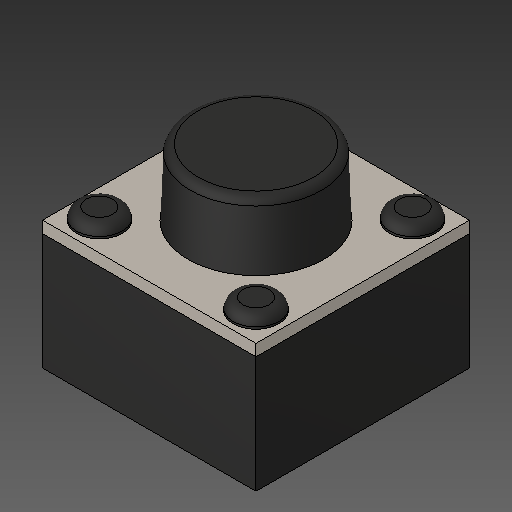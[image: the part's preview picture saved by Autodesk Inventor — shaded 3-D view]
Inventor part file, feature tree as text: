
AUTODESK INVENTOR PART (.ipt)
format: ipt  version: 2018.2 (Build 222227000, 227)  size: 160,256 bytes
history: native  units: mm
features: other x4, fillet x2
ambient origin geometry x8: Origin, YZ Plane, XZ Plane, XY Plane, X Axis, Y Axis, Z Axis, Center Point
bodies: Body1 (feature_tree), Body2 (feature_tree), Body3 (feature_tree)
feature tree (6):
  other  "ソリッド1"
  other  "ソリッド2"
  other  "ソリッド3"
  other  "Boss-Extrude2"
  fillet  "Fillet1"  [1 undecoded]
  fillet  "Fillet2"  [1 undecoded]
note: 2 required parameter values undecoded (feature->parameter linkage not recoverable at this tier; creation-order binding heuristic only, values carry confidence <= 0.55)
